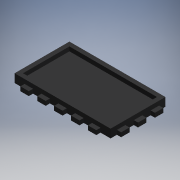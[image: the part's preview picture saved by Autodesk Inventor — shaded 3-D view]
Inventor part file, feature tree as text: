
AUTODESK INVENTOR PART (.ipt)
format: ipt  version: 2019 (Build 230136000, 136)  size: 253,440 bytes
history: native  units: mm
features: extrude x3, sketch x3, projected_geometry x1
ambient origin geometry x8: Origin, YZ Plane, XZ Plane, XY Plane, X Axis, Y Axis, Z Axis, Center Point
bodies: Solid1 (feature_tree)
feature tree (7):
  extrude  "Extrusion1"  Depth=60.0mm
  extrude  "Extrusion3"  Depth=4.0mm
  extrude  "Extrusion4"  Depth=4.0mm
  sketch  "Sketch1"  dims[d0=99.0mm d1=60.0mm]
  sketch  "Sketch3"  dims[d6=4.0mm d7=0.0mm d11=4.0mm]
  sketch  "Sketch5"  dims[d12=8.0mm d13=4.0mm d14=8.0mm d15=8.0mm d16=4.0mm d17=8.0mm d18=8.0mm d19=8.0mm d20=22.0mm d21=0.0mm d22=4.0mm d23=4.0mm d24=4.0mm d25=0.0mm]
  projected_geometry  "Projected Loop1"
